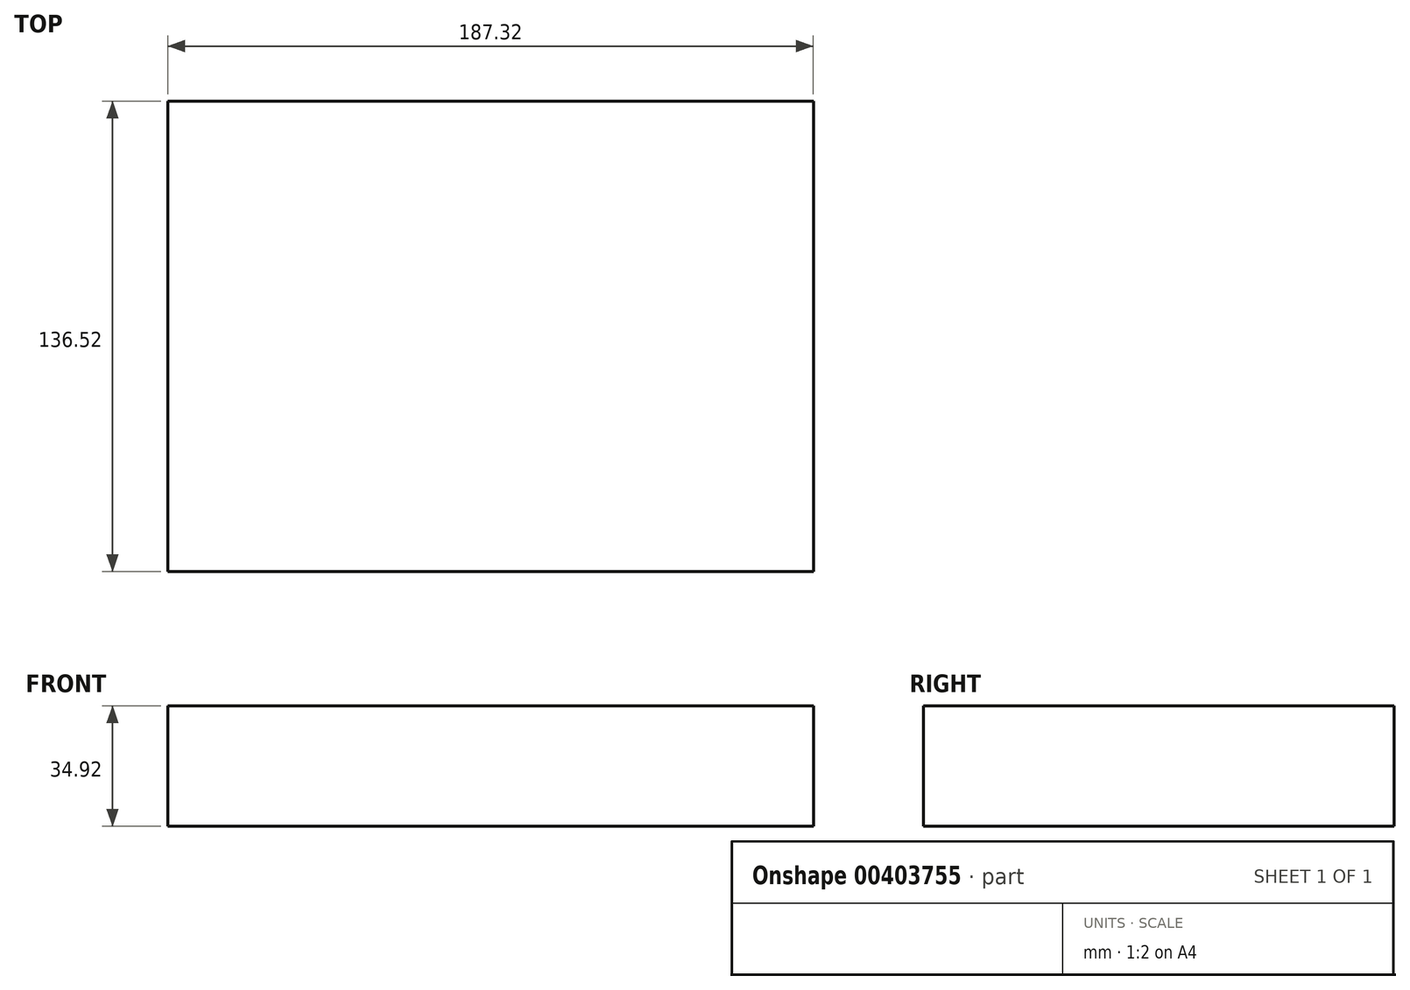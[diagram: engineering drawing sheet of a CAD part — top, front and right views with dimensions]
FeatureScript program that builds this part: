
annotation { "Feature Type Name" : "Feature", "Feature Type Description" : "" }
export const myFeature = defineFeature(function(context is Context, id is Id, definition is map)
    precondition{}
    {
        {
            var Q0;
            Q0=qCreatedBy(makeId("Top.planeOp"),FACE);
            var sketch = newSketch(context, id + "F0", { "sketchPlane" : qUnion([Q0])});
            skLineSegment(sketch, "E0.bottom", {"start": v(-93.66, 68.26) * mm, "end": v(93.66, 68.26) * mm});
            skLineSegment(sketch, "E0.top", {"start": v(-93.66, -68.26) * mm, "end": v(93.66, -68.26) * mm});
            skLineSegment(sketch, "E0.left", {"start": v(-93.66, 68.26) * mm, "end": v(-93.66, -68.26) * mm});
            skLineSegment(sketch, "E0.right", {"start": v(93.66, 68.26) * mm, "end": v(93.66, -68.26) * mm});
            skPoint(sketch, "E0.middle", {"position": v(0, 0) * mm});
            skSolve(sketch);
        }
        {
            var Q0;
            Q0 = qSketchRegion(id + "F0", true);
            extrude(context, id + "F1", {"entities" : qUnion([Q0]), "depth" : 34.92 * mm, "offsetDistance" : 25.4 * mm});
        }
    });
